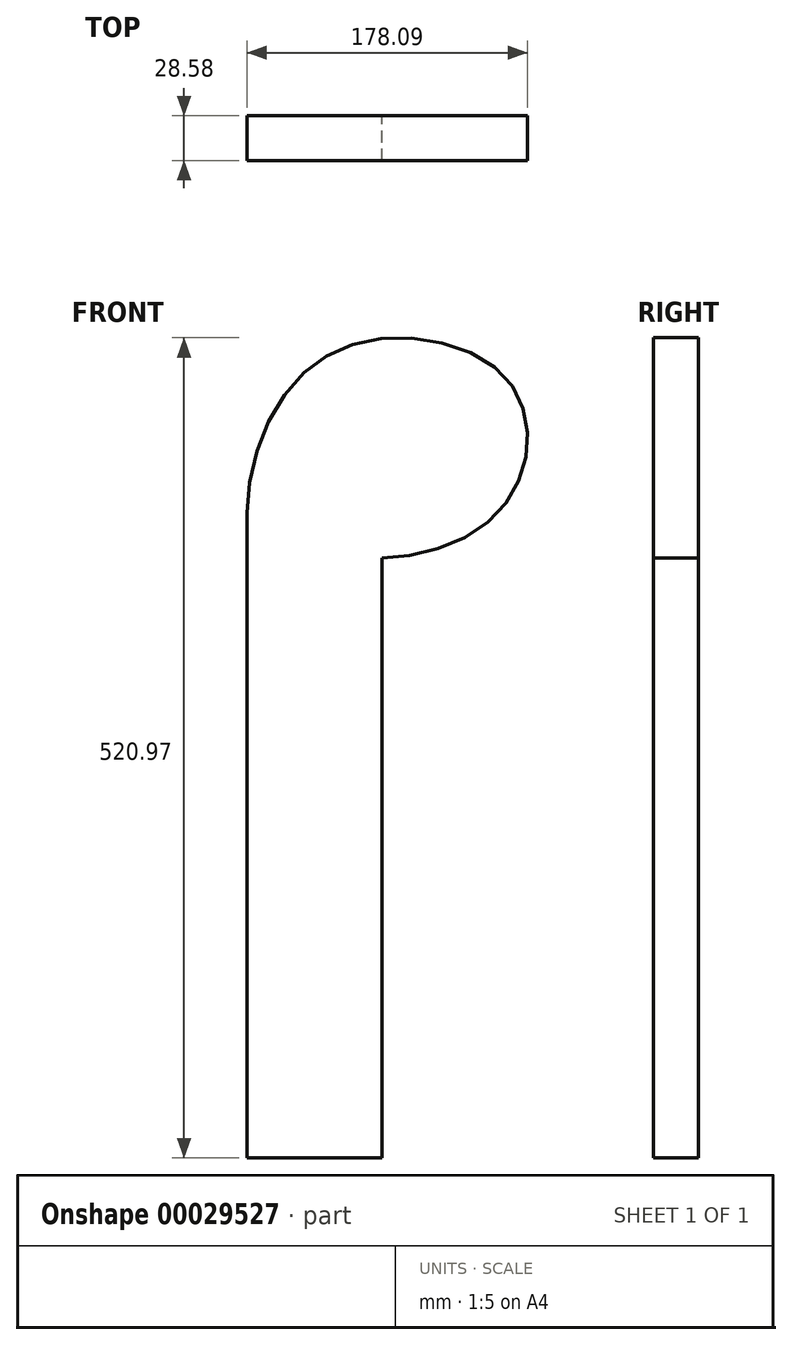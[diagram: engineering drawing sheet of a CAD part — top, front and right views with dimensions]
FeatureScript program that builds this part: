
annotation { "Feature Type Name" : "Feature", "Feature Type Description" : "" }
export const myFeature = defineFeature(function(context is Context, id is Id, definition is map)
    precondition{}
    {
        {
            var Q0;
            Q0=qCreatedBy(makeId("Front.planeOp"),FACE);
            var sketch = newSketch(context, id + "F0", { "sketchPlane" : qUnion([Q0])});
            skLineSegment(sketch, "E0", {"start": v(0, 0) * mm, "end": v(85.73, 0) * mm});
            skLineSegment(sketch, "E1", {"start": v(0, 0) * mm, "end": v(0, 409.58) * mm});
            skLineSegment(sketch, "E2", {"start": v(85.73, 0) * mm, "end": v(85.73, 381) * mm});
            skLineSegment(sketch, "E3", {"start": v(0, 409.58) * mm, "end": v(0, 520.7) * mm, "construction": true});
            skLineSegment(sketch, "E4", {"start": v(0, 520.7) * mm, "end": v(177.8, 520.7) * mm, "construction": true});
            skLineSegment(sketch, "E5", {"start": v(177.8, 520.7) * mm, "end": v(177.8, 381) * mm, "construction": true});
            skLineSegment(sketch, "E6", {"start": v(177.8, 381) * mm, "end": v(85.73, 381) * mm, "construction": true});
            skFitSpline(sketch, "E7", {"points": [v(0, 409.58) * mm, v(27.16, 489.28) * mm, v(88.9, 520.7) * mm, v(160.64, 499.4) * mm, v(177.8, 450.85) * mm, v(151.98, 403.03) * mm, v(85.73, 381) * mm], "startDerivative": vector(0, 439.4) * mm, "endDerivative": vector(-390.3, 0) * mm});
            skSolve(sketch);
        }
        {
            var Q0;
            Q0=makeQuery(id+"F0.imprint","IMPRINT",FACE,{"disambiguationData":[TD([[makeQuery(id+"F0.imprint","IMPRINT",EDGE,{"derivedFrom":sQuery(id+"F0.wireOp",EDGE,"E0")}),1.0]])]});
            extrude(context, id + "F1", {"entities" : qUnion([Q0]), "depth" : 28.57 * mm});
        }
    });
